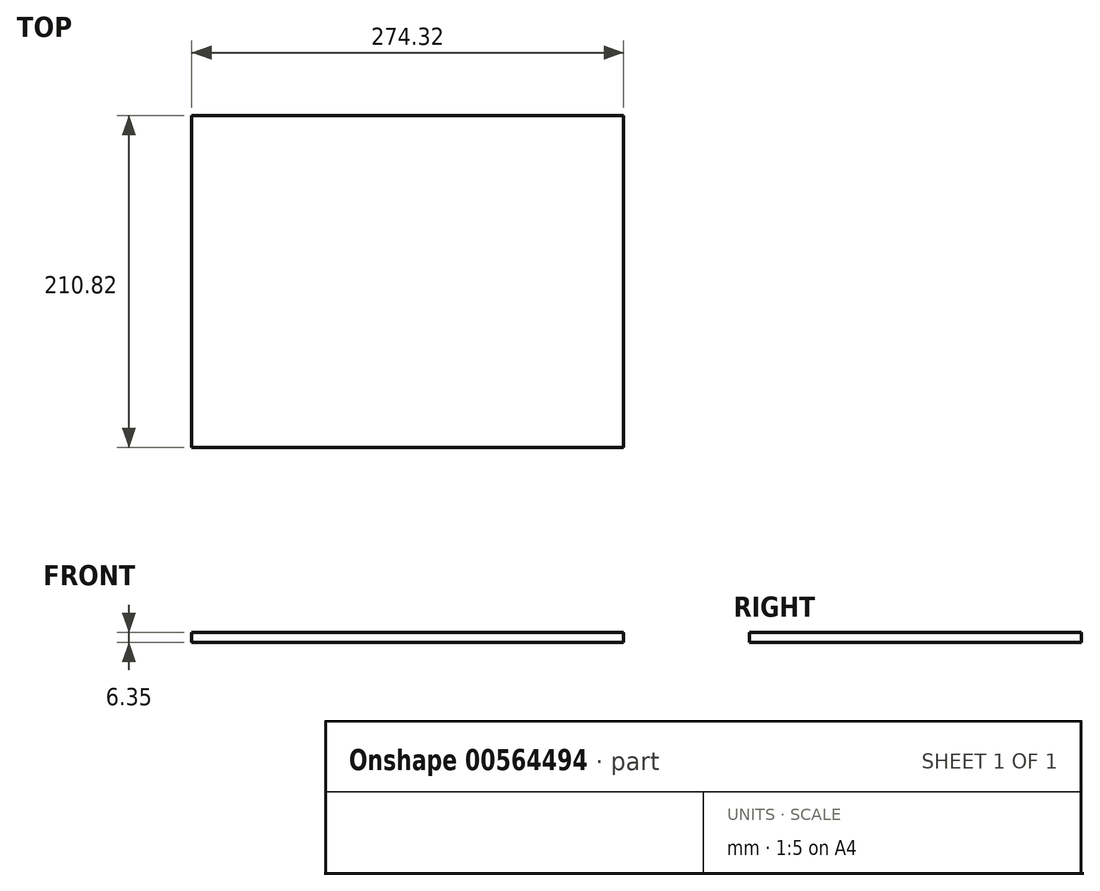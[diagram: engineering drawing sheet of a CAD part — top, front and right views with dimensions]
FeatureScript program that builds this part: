
annotation { "Feature Type Name" : "Feature", "Feature Type Description" : "" }
export const myFeature = defineFeature(function(context is Context, id is Id, definition is map)
    precondition{}
    {
        {
            var Q0;
            Q0=qCreatedBy(makeId("Top.planeOp"),FACE);
            var sketch = newSketch(context, id + "F0", { "sketchPlane" : qUnion([Q0])});
            skLineSegment(sketch, "E0.bottom", {"start": v(0, 0) * mm, "end": v(274.32, 0) * mm});
            skLineSegment(sketch, "E0.top", {"start": v(0, -210.82) * mm, "end": v(274.32, -210.82) * mm});
            skLineSegment(sketch, "E0.left", {"start": v(0, 0) * mm, "end": v(0, -210.82) * mm});
            skLineSegment(sketch, "E0.right", {"start": v(274.32, 0) * mm, "end": v(274.32, -210.82) * mm});
            skSolve(sketch);
        }
        {
            var Q0;
            Q0=makeQuery(id+"F0.imprint","IMPRINT",FACE,{"disambiguationData":[TD([[makeQuery(id+"F0.imprint","IMPRINT",EDGE,{"derivedFrom":sQuery(id+"F0.wireOp",EDGE,"E0.bottom")}),-1.0]])]});
            extrude(context, id + "F1", {"entities" : qUnion([Q0]), "depth" : 6.35 * mm, "offsetDistance" : 25.4 * mm});
        }
    });
